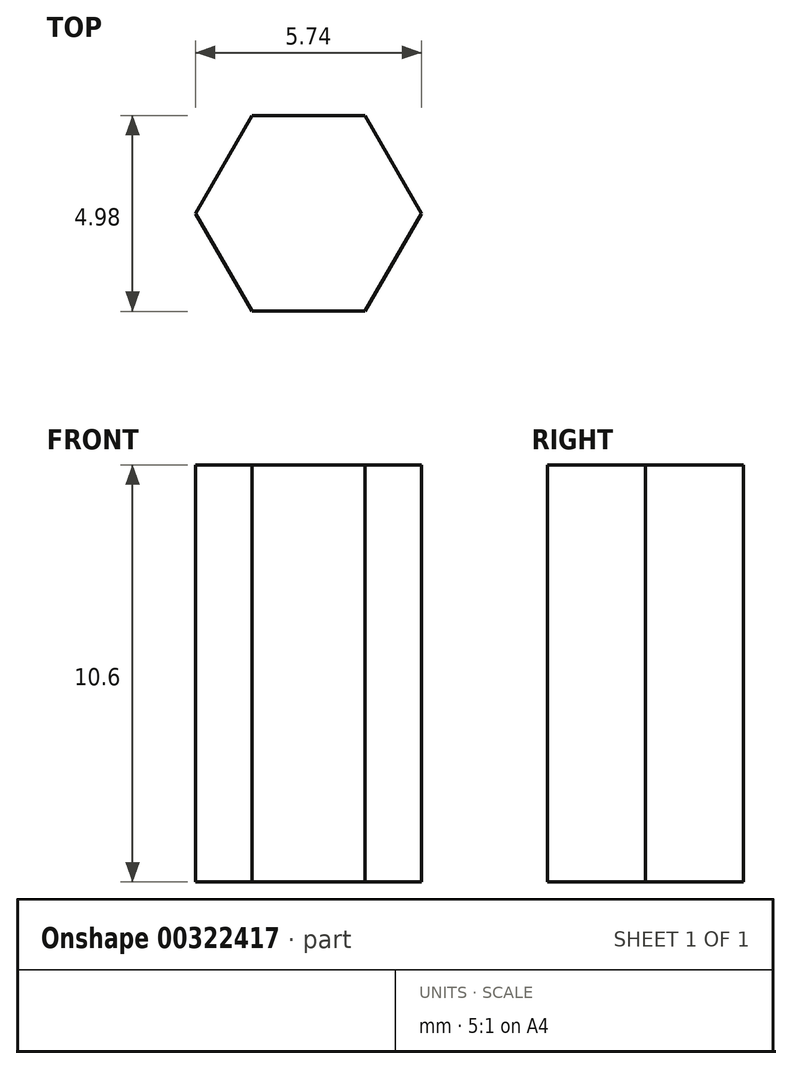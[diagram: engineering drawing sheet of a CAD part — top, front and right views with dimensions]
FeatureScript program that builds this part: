
annotation { "Feature Type Name" : "Feature", "Feature Type Description" : "" }
export const myFeature = defineFeature(function(context is Context, id is Id, definition is map)
    precondition{}
    {
        {
            var Q0;
            Q0=qCreatedBy(makeId("Top.planeOp"),FACE);
            var sketch = newSketch(context, id + "F0", { "sketchPlane" : qUnion([Q0])});
            skCircle(sketch, "E0.cCircle", {"center": v(0, 0) * mm, "radius": 2.49 * mm, "construction": true});
            skLineSegment(sketch, "E0.0", {"start": v(-1.43, 2.49) * mm, "end": v(1.43, 2.49) * mm});
            skLineSegment(sketch, "E0.1", {"start": v(1.43, 2.49) * mm, "end": v(2.87, 0) * mm});
            skLineSegment(sketch, "E0.2", {"start": v(2.87, 0) * mm, "end": v(1.44, -2.49) * mm});
            skLineSegment(sketch, "E0.3", {"start": v(1.44, -2.49) * mm, "end": v(-1.43, -2.49) * mm});
            skLineSegment(sketch, "E0.4", {"start": v(-1.43, -2.49) * mm, "end": v(-2.87, 0) * mm});
            skLineSegment(sketch, "E0.5", {"start": v(-2.87, 0) * mm, "end": v(-1.43, 2.49) * mm});
            skPoint(sketch, "E0.0.midPoint", {"position": v(0, 2.49) * mm});
            skSolve(sketch);
        }
        {
            var Q0;
            Q0 = qSketchRegion(id + "F0", true);
            extrude(context, id + "F1", {"entities" : qUnion([Q0]), "depth" : 10.6 * mm});
        }
    });
